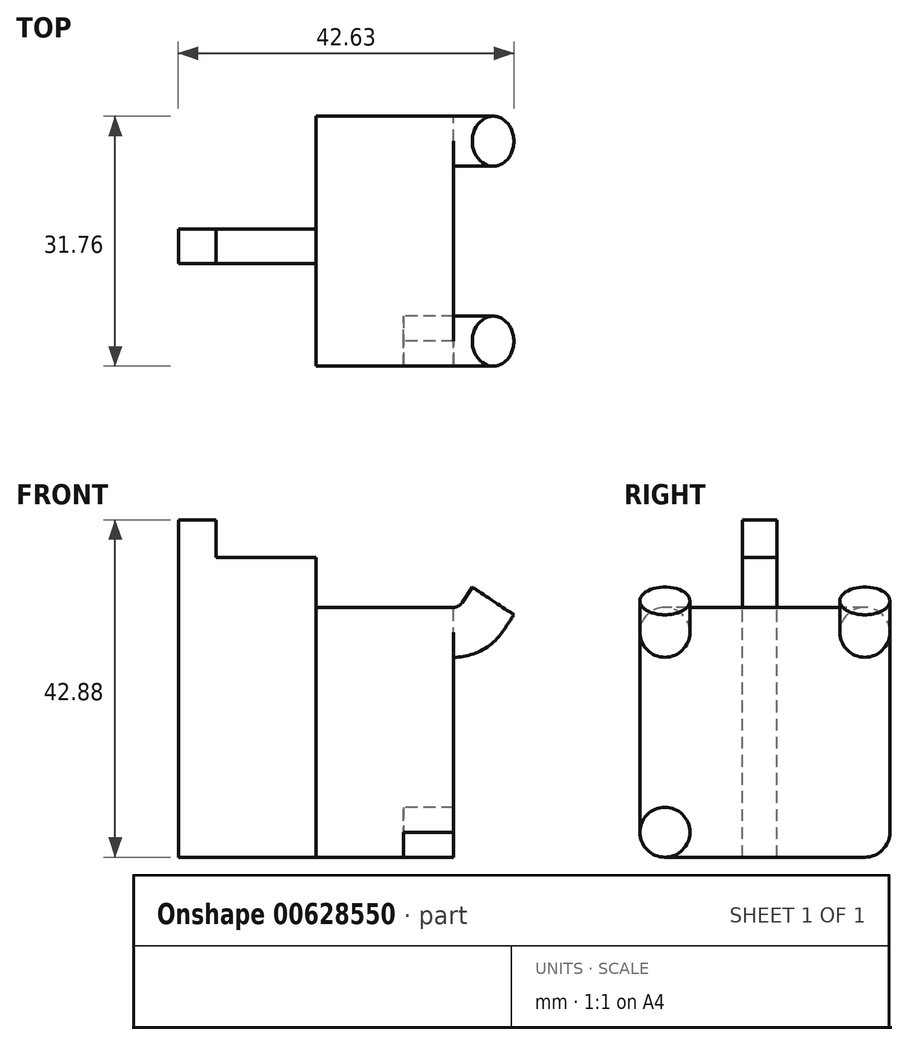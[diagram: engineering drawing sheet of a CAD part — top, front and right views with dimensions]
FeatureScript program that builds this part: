
annotation { "Feature Type Name" : "Feature", "Feature Type Description" : "" }
export const myFeature = defineFeature(function(context is Context, id is Id, definition is map)
    precondition{}
    {
        {
            var Q0;
            Q0=qCreatedBy(makeId("Right.planeOp"),FACE);
            var sketch = newSketch(context, id + "F0", { "sketchPlane" : qUnion([Q0])});
            skLineSegment(sketch, "E0.bottom", {"start": v(15.88, -15.87) * mm, "end": v(-15.88, -15.88) * mm});
            skLineSegment(sketch, "E0.top", {"start": v(15.88, 15.88) * mm, "end": v(-15.88, 15.88) * mm});
            skLineSegment(sketch, "E0.left", {"start": v(15.88, -15.87) * mm, "end": v(15.88, 15.88) * mm});
            skLineSegment(sketch, "E0.right", {"start": v(-15.88, -15.88) * mm, "end": v(-15.88, 15.88) * mm});
            skPoint(sketch, "E0.middle", {"position": v(0, 0) * mm});
            skSolve(sketch);
        }
        {
            var Q0;
            Q0=makeQuery(id+"F0.imprint","IMPRINT",FACE,{"disambiguationData":[TD([[makeQuery(id+"F0.imprint","IMPRINT",EDGE,{"derivedFrom":sQuery(id+"F0.wireOp",EDGE,"E0.bottom")}),-1.0]])]});
            extrude(context, id + "F1", {"entities" : qUnion([Q0]), "depth" : 11.13 * mm, "offsetDistance" : 25.4 * mm});
        }
        {
            var Q0;
            Q0=makeQuery(id+"F1.opExtrude","CAP_FACE",FACE,{"disambiguationData":[OSD([sQuery(id+"F0.wireOp",EDGE,"E0.bottom"),sQuery(id+"F0.wireOp",EDGE,"E0.top"),sQuery(id+"F0.wireOp",EDGE,"E0.left"),sQuery(id+"F0.wireOp",EDGE,"E0.right")])],"isStart":false});
            var sketch = newSketch(context, id + "F2", { "sketchPlane" : qUnion([Q0])});
            skCircle(sketch, "E1", {"center": v(-12.7, 12.7) * mm, "radius": 3.18 * mm});
            skLineSegment(sketch, "E2", {"start": v(-24.57, 0) * mm, "end": v(19.39, 0) * mm, "construction": true});
            skPoint(sketch, "E2.endSnap0", {"position": v(-15.88, 0) * mm});
            skLineSegment(sketch, "E3", {"start": v(0, 20.38) * mm, "end": v(0, -18.88) * mm, "construction": true});
            skCircle(sketch, "E4.MirrorC", {"center": v(-12.7, -12.7) * mm, "radius": 3.18 * mm});
            skLineSegment(sketch, "E5.MirrorCS", {"start": v(0, -20.38) * mm, "end": v(0, 18.88) * mm, "construction": true});
            skCircle(sketch, "E6.MirrorC", {"center": v(12.7, 12.7) * mm, "radius": 3.18 * mm});
            skCircle(sketch, "E7.MirrorC", {"center": v(12.7, -12.7) * mm, "radius": 3.18 * mm});
            skLineSegment(sketch, "E8", {"start": v(-12.7, 15.88) * mm, "end": v(-12.7, -15.88) * mm, "construction": true});
            skLineSegment(sketch, "E9", {"start": v(-15.88, 12.7) * mm, "end": v(15.88, 12.7) * mm, "construction": true});
            skPoint(sketch, "E10", {"position": v(-12.7, 15.88) * mm});
            skPoint(sketch, "E11", {"position": v(0, 0) * mm});
            skSolve(sketch);
        }
        {
            var Q0;
            Q0=makeQuery(id+"F1.opExtrude","SWEPT_FACE",FACE,{"disambiguationData":[OSD([sQuery(id+"F0.wireOp",EDGE,"E0.top")])]});
            var sketch = newSketch(context, id + "F3", { "sketchPlane" : qUnion([Q0])});
            skLineSegment(sketch, "E12", {"start": v(0, -12.7) * mm, "end": v(11.13, -12.7) * mm, "construction": true});
            skSolve(sketch);
        }
        {
            var Q0;
            Q0=sQuery(id+"F3.wireOp",VERTEX,"E12.start");
            var Q1;
            Q1=sQuery(id+"F2.wireOp",VERTEX,"E10");
            var Q2;
            Q2=sQuery(id+"F2.wireOp",VERTEX,"E8.end");
            cPlane(context, id + "F4", {"entities" : qUnion([Q0, Q1, Q2]), "cplaneType" : CPlaneType.THREE_POINT, "offset" : 25.4 * mm, "width" : 152.4 * mm, "height" : 152.4 * mm});
        }
        {
            var Q0;
            Q0=qCreatedBy(id+"F4.planeOp",FACE);
            var sketch = newSketch(context, id + "F5", { "sketchPlane" : qUnion([Q0])});
            skLineSegment(sketch, "E13", {"start": v(11.13, 9.53) * mm, "end": v(11.13, 15.88) * mm});
            skLineSegment(sketch, "E14", {"start": v(11.13, 9.53) * mm, "end": v(17.48, 9.53) * mm});
            skArc(sketch, "E15", {"start": v(17.48, 9.53) * mm, "mid": v(21.08, 10.43) * mm, "end": v(23.83, 12.93) * mm});
            skLineSegment(sketch, "E16", {"start": v(23.83, 12.93) * mm, "end": v(25.15, 14.93) * mm});
            skSolve(sketch);
        }
        {
            var Q0;
            {var subQ0=sQuery(id+"F2.wireOp",EDGE,"E1");var subQ1=makeQuery(id+"F2.imprint","INTERSECT",VERTEX,{"derivedFrom":[makeQuery(id+"F1.opExtrude","CAP_EDGE",EDGE,{"disambiguationData":[OSD([sQuery(id+"F0.wireOp",EDGE,"E0.top")])],"isStart":false}),subQ0]});Q0=makeQuery(id+"F2.imprint","IMPRINT",FACE,{"disambiguationData":[TD([[makeQuery(id+"F2.imprint","IMPRINT",EDGE,{"disambiguationData":[TD([[subQ1,-1.0]])],"derivedFrom":subQ0}),1.0]])]});}
            var Q1;
            Q1=qSketchRegion(id+"F5",true);
            var Q2;
            Q2=sQuery(id+"F5.wireOp",EDGE,"E14");
            var Q3;
            Q3=sQuery(id+"F5.wireOp",EDGE,"E15");
            var Q4;
            Q4=sQuery(id+"F5.wireOp",EDGE,"E16");
            sweep(context, id + "F6", {"operationType" : NewBodyOperationType.ADD, "profiles" : qUnion([Q0, Q1]), "path" : qUnion([Q2, Q3, Q4])});
        }
        {
            var Q0;
            {var subQ0=sQuery(id+"F0.wireOp",EDGE,"E0.top");Q0=makeQuery(id+"F3.imprint","IMPRINT",FACE,{"disambiguationData":[TD([[makeQuery(id+"F3.imprint","IMPRINT",EDGE,{"derivedFrom":makeQuery(id+"F1.opExtrude","CAP_EDGE",EDGE,{"disambiguationData":[OSD([subQ0])],"isStart":true})}),1.0]])]});}
            var sketch = newSketch(context, id + "F7", { "sketchPlane" : qUnion([Q0])});
            skLineSegment(sketch, "E17", {"start": v(12.55, 0) * mm, "end": v(0, 0) * mm, "construction": true});
            skSolve(sketch);
        }
        {
            var Q0;
            Q0=sQuery(id+"F7.wireOp",VERTEX,"E17.end");
            var Q1;
            Q1=sQuery(id+"F7.wireOp",VERTEX,"E17.start");
            var Q2;
            Q2=sQuery(id+"F2.wireOp",VERTEX,"E11");
            cPlane(context, id + "F8", {"entities" : qUnion([Q0, Q1, Q2]), "cplaneType" : CPlaneType.THREE_POINT, "offset" : 25.4 * mm, "width" : 152.4 * mm, "height" : 152.4 * mm});
        }
        {
            var Q0;
            Q0=makeQuery(id+"F1.opExtrude","SWEPT_BODY",BODY,{"disambiguationData":[OSD([sQuery(id+"F0.wireOp",EDGE,"E0.bottom"),sQuery(id+"F0.wireOp",EDGE,"E0.top"),sQuery(id+"F0.wireOp",EDGE,"E0.left"),sQuery(id+"F0.wireOp",EDGE,"E0.right")])]});
            var Q1;
            Q1=qCreatedBy(id+"F8.planeOp",FACE);
            mirror(context, id + "F9", {"operationType" : NewBodyOperationType.ADD, "entities" : qUnion([Q0]), "mirrorPlane" : qUnion([Q1])});
        }
        {
            var Q0;
            {var subQ0=sQuery(id+"F2.wireOp",EDGE,"E4.MirrorC");var subQ1=makeQuery(id+"F2.imprint","INTERSECT",VERTEX,{"derivedFrom":[makeQuery(id+"F1.opExtrude","CAP_EDGE",EDGE,{"disambiguationData":[OSD([sQuery(id+"F0.wireOp",EDGE,"E0.bottom")])],"isStart":false}),subQ0]});Q0=makeQuery(id+"F2.imprint","IMPRINT",FACE,{"disambiguationData":[TD([[makeQuery(id+"F2.imprint","IMPRINT",EDGE,{"disambiguationData":[TD([[subQ1,-1.0]])],"derivedFrom":subQ0}),-1.0]])]});}
            var Q1;
            {var subQ0=sQuery(id+"F2.wireOp",EDGE,"E7.MirrorC");var subQ1=makeQuery(id+"F2.imprint","INTERSECT",VERTEX,{"derivedFrom":[makeQuery(id+"F1.opExtrude","CAP_EDGE",EDGE,{"disambiguationData":[OSD([sQuery(id+"F0.wireOp",EDGE,"E0.bottom")])],"isStart":false}),subQ0]});Q1=makeQuery(id+"F2.imprint","IMPRINT",FACE,{"disambiguationData":[TD([[makeQuery(id+"F2.imprint","IMPRINT",EDGE,{"disambiguationData":[TD([[subQ1,-1.0]])],"derivedFrom":subQ0}),1.0]])]});}
            extrude(context, id + "F10", {"entities" : qUnion([Q0, Q1]), "operationType" : NewBodyOperationType.ADD, "depth" : 6.35 * mm, "offsetDistance" : 25.4 * mm});
        }
        {
            var Q0;
            Q0=makeQuery(id+"F1.opExtrude","SWEPT_EDGE",EDGE,{"disambiguationData":[OSD([sQuery(id+"F0.wireOp",EDGE,"E0.top"),sQuery(id+"F0.wireOp",EDGE,"E0.right")])]});
            var Q1;
            Q1=makeQuery(id+"F1.opExtrude","SWEPT_EDGE",EDGE,{"disambiguationData":[OSD([sQuery(id+"F0.wireOp",EDGE,"E0.bottom"),sQuery(id+"F0.wireOp",EDGE,"E0.right")])]});
            var Q2;
            Q2=makeQuery(id+"F1.opExtrude","SWEPT_EDGE",EDGE,{"disambiguationData":[OSD([sQuery(id+"F0.wireOp",EDGE,"E0.bottom"),sQuery(id+"F0.wireOp",EDGE,"E0.left")])]});
            var Q3;
            Q3=makeQuery(id+"F1.opExtrude","SWEPT_EDGE",EDGE,{"disambiguationData":[OSD([sQuery(id+"F0.wireOp",EDGE,"E0.top"),sQuery(id+"F0.wireOp",EDGE,"E0.left")])]});
            fillet(context, id + "F11", {"entities" : qUnion([Q0, Q1, Q2, Q3]), "radius" : 3.17 * mm, "tangentPropagation" : true, "allowEdgeOverflow" : false});
        }
        {
            var Q0;
            Q0=makeQuery(id+"F1.opExtrude","CAP_FACE",FACE,{"disambiguationData":[OSD([sQuery(id+"F0.wireOp",EDGE,"E0.bottom"),sQuery(id+"F0.wireOp",EDGE,"E0.top"),sQuery(id+"F0.wireOp",EDGE,"E0.left"),sQuery(id+"F0.wireOp",EDGE,"E0.right")])],"isStart":true});
            var sketch = newSketch(context, id + "F12", { "sketchPlane" : qUnion([Q0])});
            skPoint(sketch, "E18.middle", {"position": v(0, 0) * mm});
            skLineSegment(sketch, "E19.bottom", {"start": v(-1.52, -15.87) * mm, "end": v(2.84, -15.87) * mm});
            skLineSegment(sketch, "E19.top", {"start": v(-1.52, 22.23) * mm, "end": v(2.84, 22.23) * mm});
            skLineSegment(sketch, "E19.left", {"start": v(-1.52, -15.88) * mm, "end": v(-1.52, 22.23) * mm});
            skLineSegment(sketch, "E19.right", {"start": v(2.84, -15.88) * mm, "end": v(2.84, 22.23) * mm});
            skSolve(sketch);
        }
        {
            var Q0;
            {var subQ0=sQuery(id+"F12.wireOp",EDGE,"E19.top");Q0=makeQuery(id+"F12.imprint","IMPRINT",FACE,{"disambiguationData":[TD([[makeQuery(id+"F12.imprint","IMPRINT",EDGE,{"derivedFrom":subQ0}),-1.0]])]});}
            var Q1;
            {var subQ0=sQuery(id+"F12.wireOp",EDGE,"E19.bottom");Q1=makeQuery(id+"F12.imprint","IMPRINT",FACE,{"disambiguationData":[TD([[makeQuery(id+"F12.imprint","IMPRINT",EDGE,{"derivedFrom":subQ0}),1.0]])]});}
            extrude(context, id + "F13", {"entities" : qUnion([Q0, Q1]), "operationType" : NewBodyOperationType.ADD, "depth" : 17.48 * mm, "offsetDistance" : 25.4 * mm});
        }
        {
            var Q0;
            Q0=makeQuery(id+"F13.opExtrude","SWEPT_FACE",FACE,{"disambiguationData":[OSD([sQuery(id+"F12.wireOp",EDGE,"E19.top")])]});
            var sketch = newSketch(context, id + "F14", { "sketchPlane" : qUnion([Q0])});
            skLineSegment(sketch, "E20.bottom", {"start": v(-17.48, -2.84) * mm, "end": v(-12.7, -2.84) * mm});
            skLineSegment(sketch, "E20.top", {"start": v(-17.48, 1.52) * mm, "end": v(-12.7, 1.52) * mm});
            skLineSegment(sketch, "E20.left", {"start": v(-17.48, -2.84) * mm, "end": v(-17.48, 1.52) * mm});
            skLineSegment(sketch, "E20.right", {"start": v(-12.7, -2.84) * mm, "end": v(-12.7, 1.52) * mm});
            skSolve(sketch);
        }
        {
            var Q0;
            Q0=makeQuery(id+"F14.imprint","IMPRINT",FACE,{"disambiguationData":[TD([[makeQuery(id+"F14.imprint","IMPRINT",EDGE,{"derivedFrom":sQuery(id+"F14.wireOp",EDGE,"E20.bottom")}),1.0]])]});
            extrude(context, id + "F15", {"entities" : qUnion([Q0]), "operationType" : NewBodyOperationType.ADD, "depth" : 4.78 * mm, "offsetDistance" : 25.4 * mm});
        }
    });
